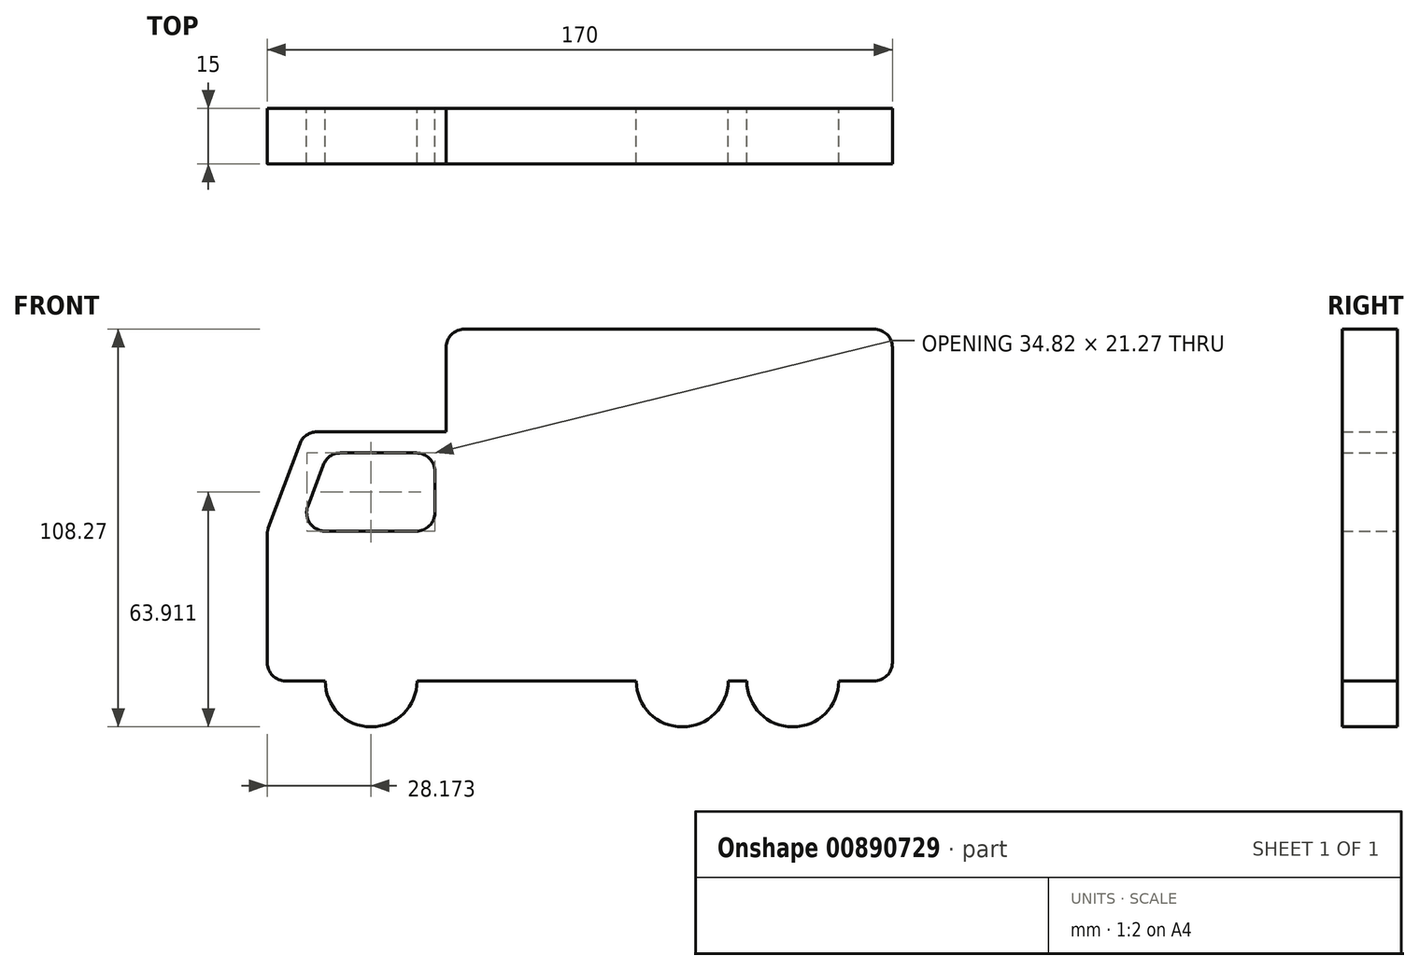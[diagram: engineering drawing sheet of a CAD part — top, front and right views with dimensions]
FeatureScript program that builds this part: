
annotation { "Feature Type Name" : "Feature", "Feature Type Description" : "" }
export const myFeature = defineFeature(function(context is Context, id is Id, definition is map)
    precondition{}
    {
        {
            var Q0;
            Q0=qCreatedBy(makeId("Front.planeOp"),FACE);
            var sketch = newSketch(context, id + "F0", { "sketchPlane" : qUnion([Q0])});
            skLineSegment(sketch, "E0.bottom", {"start": v(-68.88, 39.56) * mm, "end": v(-33.75, 39.56) * mm});
            skLineSegment(sketch, "E0.top", {"start": v(-77.42, -28.2) * mm, "end": v(-66.66, -28.2) * mm});
            skLineSegment(sketch, "E0.left", {"start": v(-82.42, 11.67) * mm, "end": v(-82.42, -23.2) * mm});
            skLineSegment(sketch, "E1.bottom", {"start": v(-33.75, -28.2) * mm, "end": v(17.97, -28.2) * mm});
            skLineSegment(sketch, "E1.top", {"start": v(-28.75, 67.56) * mm, "end": v(82.58, 67.56) * mm});
            skLineSegment(sketch, "E1.left", {"start": v(-33.75, 39.56) * mm, "end": v(-33.75, 62.56) * mm});
            skLineSegment(sketch, "E1.right", {"start": v(87.58, -23.2) * mm, "end": v(87.58, 62.56) * mm});
            skLineSegment(sketch, "E2", {"start": v(-82.1, 13.41) * mm, "end": v(-73.57, 36.3) * mm});
            skArc(sketch, "E3", {"start": v(-66.66, -28.2) * mm, "mid": v(-54.16, -40.7) * mm, "end": v(-41.66, -28.2) * mm});
            skArc(sketch, "E4", {"start": v(17.97, -28.2) * mm, "mid": v(30.47, -40.7) * mm, "end": v(42.97, -28.2) * mm});
            skArc(sketch, "E5", {"start": v(48, -28.2) * mm, "mid": v(60.5, -40.7) * mm, "end": v(73, -28.2) * mm});
            skLineSegment(sketch, "E6.trimOffspring", {"start": v(-41.66, -28.2) * mm, "end": v(-33.75, -28.2) * mm});
            skLineSegment(sketch, "E7.trimOffspring", {"start": v(42.97, -28.2) * mm, "end": v(48, -28.2) * mm});
            skLineSegment(sketch, "E8.trimOffspring", {"start": v(73, -28.2) * mm, "end": v(82.58, -28.2) * mm});
            skLineSegment(sketch, "E9", {"start": v(-62.49, 33.83) * mm, "end": v(-41.84, 33.83) * mm});
            skLineSegment(sketch, "E10", {"start": v(-36.84, 28.83) * mm, "end": v(-36.84, 17.57) * mm});
            skLineSegment(sketch, "E11", {"start": v(-41.84, 12.57) * mm, "end": v(-66.69, 12.57) * mm});
            skLineSegment(sketch, "E12", {"start": v(-71.37, 19.32) * mm, "end": v(-67.17, 30.58) * mm});
            skPoint(sketch, "E13.visualSharp", {"position": v(-82.42, -28.2) * mm});
            skArc(sketch, "E13.filletArc", {"start": v(-82.42, -23.2) * mm, "mid": v(-80.95, -26.75) * mm, "end": v(-77.42, -28.2) * mm});
            skPoint(sketch, "E14.visualSharp", {"position": v(-33.75, 67.56) * mm});
            skArc(sketch, "E14.filletArc", {"start": v(-28.75, 67.56) * mm, "mid": v(-32.29, 66.1) * mm, "end": v(-33.75, 62.56) * mm});
            skPoint(sketch, "E15.visualSharp", {"position": v(87.58, 67.56) * mm});
            skArc(sketch, "E15.filletArc", {"start": v(87.58, 62.56) * mm, "mid": v(86.12, 66.1) * mm, "end": v(82.58, 67.56) * mm});
            skPoint(sketch, "E16.visualSharp", {"position": v(87.58, -28.2) * mm});
            skArc(sketch, "E16.filletArc", {"start": v(82.58, -28.2) * mm, "mid": v(86.12, -26.75) * mm, "end": v(87.58, -23.2) * mm});
            skPoint(sketch, "E17.visualSharp", {"position": v(-82.42, 12.57) * mm});
            skArc(sketch, "E17.filletArc", {"start": v(-82.1, 13.41) * mm, "mid": v(-82.34, 12.55) * mm, "end": v(-82.42, 11.67) * mm});
            skPoint(sketch, "E18.visualSharp", {"position": v(-72.35, 39.56) * mm});
            skArc(sketch, "E18.filletArc", {"start": v(-68.88, 39.56) * mm, "mid": v(-71.73, 38.67) * mm, "end": v(-73.57, 36.3) * mm});
            skPoint(sketch, "E19.visualSharp", {"position": v(-73.89, 12.57) * mm});
            skArc(sketch, "E19.filletArc", {"start": v(-71.37, 19.32) * mm, "mid": v(-70.8, 14.72) * mm, "end": v(-66.69, 12.57) * mm});
            skPoint(sketch, "E20.visualSharp", {"position": v(-65.96, 33.83) * mm});
            skArc(sketch, "E20.filletArc", {"start": v(-62.49, 33.83) * mm, "mid": v(-65.34, 32.94) * mm, "end": v(-67.17, 30.58) * mm});
            skPoint(sketch, "E21.visualSharp", {"position": v(-36.84, 33.83) * mm});
            skArc(sketch, "E21.filletArc", {"start": v(-36.84, 28.83) * mm, "mid": v(-38.3, 32.37) * mm, "end": v(-41.84, 33.83) * mm});
            skPoint(sketch, "E22.visualSharp", {"position": v(-36.84, 12.57) * mm});
            skArc(sketch, "E22.filletArc", {"start": v(-41.84, 12.57) * mm, "mid": v(-38.3, 14.03) * mm, "end": v(-36.84, 17.57) * mm});
            skSolve(sketch);
        }
        {
            var Q0;
            Q0=makeQuery(id+"F0.imprint","IMPRINT",FACE,{"disambiguationData":[TD([[makeQuery(id+"F0.imprint","IMPRINT",EDGE,{"derivedFrom":sQuery(id+"F0.wireOp",EDGE,"E0.bottom")}),-1.0]])]});
            extrude(context, id + "F1", {"entities" : qUnion([Q0]), "depth" : 15 * mm, "offsetDistance" : 25 * mm});
        }
    });
